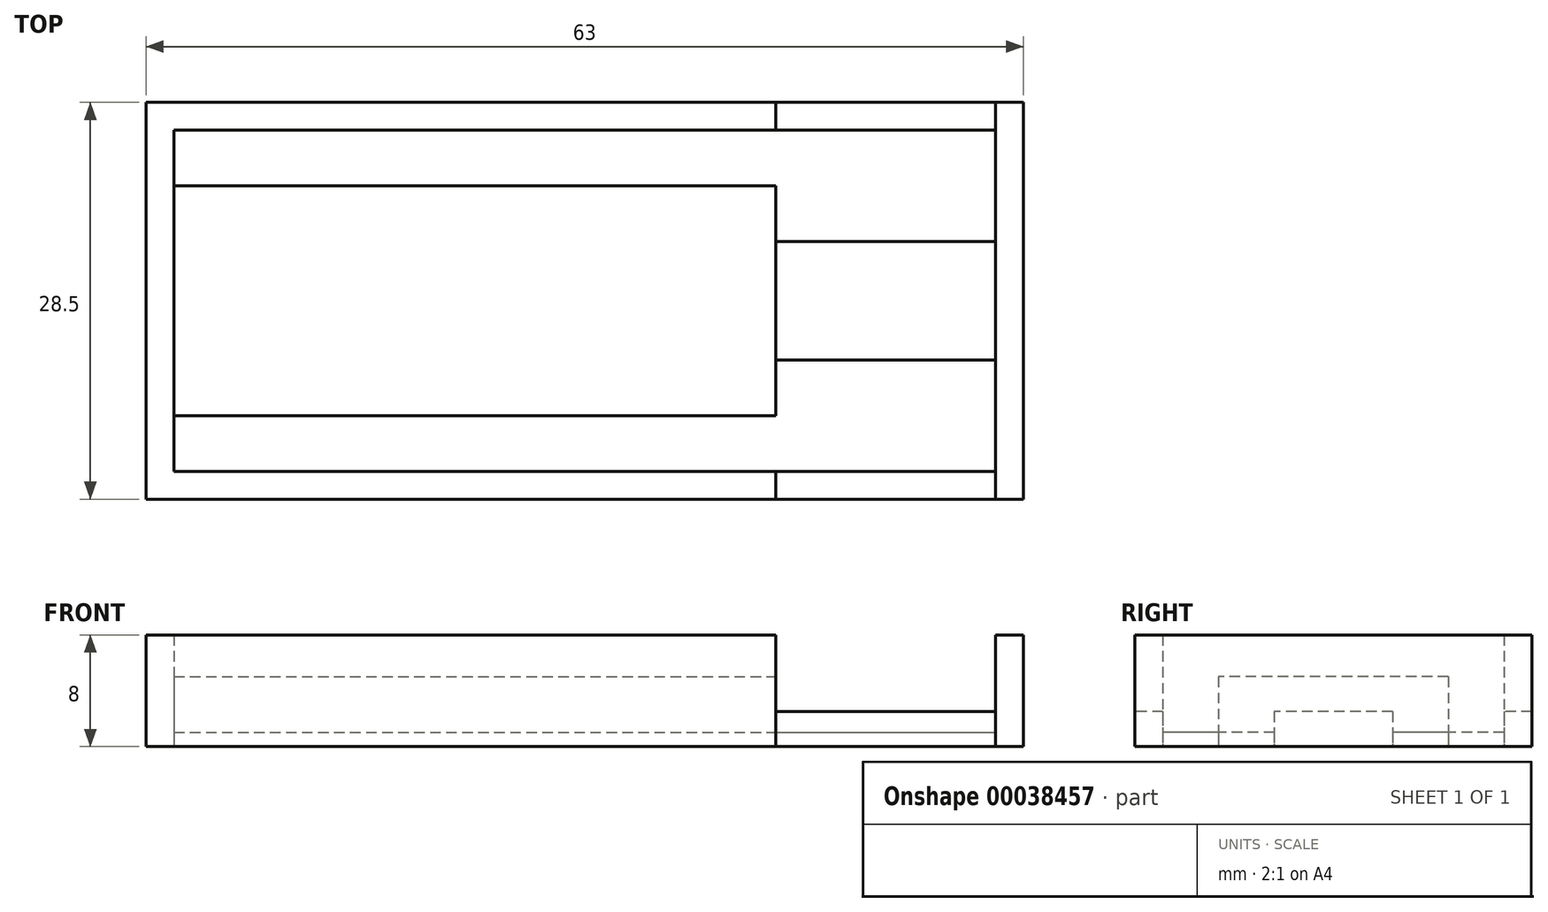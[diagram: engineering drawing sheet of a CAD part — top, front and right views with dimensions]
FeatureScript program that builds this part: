
annotation { "Feature Type Name" : "Feature", "Feature Type Description" : "" }
export const myFeature = defineFeature(function(context is Context, id is Id, definition is map)
    precondition{}
    {
        {
            var Q0;
            Q0=qCreatedBy(makeId("Top.planeOp"),FACE);
            var sketch = newSketch(context, id + "F0", { "sketchPlane" : qUnion([Q0])});
            skLineSegment(sketch, "E0", {"start": v(-83.28, 24.5) * mm, "end": v(93.04, 24.5) * mm, "construction": true});
            skLineSegment(sketch, "E1", {"start": v(59, -21.37) * mm, "end": v(59, 62.02) * mm, "construction": true});
            skLineSegment(sketch, "E2", {"start": v(-82.03, 20.5) * mm, "end": v(90.12, 20.5) * mm, "construction": true});
            skLineSegment(sketch, "E3", {"start": v(-82.58, 4) * mm, "end": v(90.12, 4) * mm, "construction": true});
            skLineSegment(sketch, "E4", {"start": v(43.2, 55.46) * mm, "end": v(43.2, -21.13) * mm, "construction": true});
            skLineSegment(sketch, "E5", {"start": v(-2, 34.22) * mm, "end": v(-2, -12.72) * mm, "construction": true});
            skLineSegment(sketch, "E6", {"start": v(-8.23, 26.5) * mm, "end": v(67.64, 26.5) * mm, "construction": true});
            skLineSegment(sketch, "E7", {"start": v(61, 36.16) * mm, "end": v(61, -15.62) * mm, "construction": true});
            skLineSegment(sketch, "E8", {"start": v(68.06, -2) * mm, "end": v(-8.92, -2) * mm, "construction": true});
            skLineSegment(sketch, "E9", {"start": v(34.9, 16.5) * mm, "end": v(73.13, 16.5) * mm, "construction": true});
            skLineSegment(sketch, "E10", {"start": v(34.68, 8) * mm, "end": v(73.78, 8) * mm, "construction": true});
            skLineSegment(sketch, "E11.bottom", {"start": v(59, 26.5) * mm, "end": v(61, 26.5) * mm});
            skLineSegment(sketch, "E11.top", {"start": v(59, -2) * mm, "end": v(61, -2) * mm});
            skLineSegment(sketch, "E11.left", {"start": v(59, 26.5) * mm, "end": v(59, -2) * mm});
            skLineSegment(sketch, "E11.right", {"start": v(61, 26.5) * mm, "end": v(61, -2) * mm});
            skLineSegment(sketch, "E12.bottom", {"start": v(43.2, 26.5) * mm, "end": v(59, 26.5) * mm});
            skLineSegment(sketch, "E12.top", {"start": v(43.2, 24.5) * mm, "end": v(59, 24.5) * mm});
            skLineSegment(sketch, "E12.left", {"start": v(43.2, 26.5) * mm, "end": v(43.2, 24.5) * mm});
            skLineSegment(sketch, "E12.right", {"start": v(59, 26.5) * mm, "end": v(59, 24.5) * mm});
            skLineSegment(sketch, "E13.top", {"start": v(43.2, 16.5) * mm, "end": v(59, 16.5) * mm});
            skLineSegment(sketch, "E13.left", {"start": v(43.2, 24.5) * mm, "end": v(43.2, 16.5) * mm});
            skLineSegment(sketch, "E13.right", {"start": v(59, 24.5) * mm, "end": v(59, 16.5) * mm});
            skLineSegment(sketch, "E14.top", {"start": v(43.2, 8) * mm, "end": v(59, 8) * mm});
            skLineSegment(sketch, "E14.left", {"start": v(43.2, 16.5) * mm, "end": v(43.2, 8) * mm});
            skLineSegment(sketch, "E14.right", {"start": v(59, 16.5) * mm, "end": v(59, 8) * mm});
            skLineSegment(sketch, "E15.top", {"start": v(43.2, 0) * mm, "end": v(59, 0) * mm});
            skLineSegment(sketch, "E15.left", {"start": v(43.2, 8) * mm, "end": v(43.2, 0) * mm});
            skLineSegment(sketch, "E15.right", {"start": v(59, 8) * mm, "end": v(59, 0) * mm});
            skLineSegment(sketch, "E16.top", {"start": v(43.2, -2) * mm, "end": v(59, -2) * mm});
            skLineSegment(sketch, "E16.left", {"start": v(43.2, 0) * mm, "end": v(43.2, -2) * mm});
            skLineSegment(sketch, "E16.right", {"start": v(59, 0) * mm, "end": v(59, -2) * mm});
            skLineSegment(sketch, "E17.bottom", {"start": v(0, 24.5) * mm, "end": v(43.2, 24.5) * mm});
            skLineSegment(sketch, "E17.top", {"start": v(0, 20.5) * mm, "end": v(43.2, 20.5) * mm});
            skLineSegment(sketch, "E17.left", {"start": v(0, 24.5) * mm, "end": v(0, 20.5) * mm});
            skLineSegment(sketch, "E17.right", {"start": v(43.2, 24.5) * mm, "end": v(43.2, 20.5) * mm});
            skLineSegment(sketch, "E18.top", {"start": v(0, 4) * mm, "end": v(43.2, 4) * mm});
            skLineSegment(sketch, "E18.left", {"start": v(0, 20.5) * mm, "end": v(0, 4) * mm});
            skLineSegment(sketch, "E18.right", {"start": v(43.2, 20.5) * mm, "end": v(43.2, 4) * mm});
            skLineSegment(sketch, "E19.top", {"start": v(0, 0) * mm, "end": v(43.2, 0) * mm});
            skLineSegment(sketch, "E19.left", {"start": v(0, 4) * mm, "end": v(0, 0) * mm});
            skLineSegment(sketch, "E19.right", {"start": v(43.2, 4) * mm, "end": v(43.2, 0) * mm});
            skLineSegment(sketch, "E20", {"start": v(43.2, 26.5) * mm, "end": v(-2, 26.5) * mm});
            skLineSegment(sketch, "E21", {"start": v(-2, 26.5) * mm, "end": v(-2, -2) * mm});
            skLineSegment(sketch, "E22", {"start": v(-2, -2) * mm, "end": v(43.2, -2) * mm});
            skSolve(sketch);
        }
        {
            var Q0;
            Q0=makeQuery(id+"F0.imprint","IMPRINT",FACE,{"disambiguationData":[TD([[makeQuery(id+"F0.imprint","IMPRINT",EDGE,{"derivedFrom":sQuery(id+"F0.wireOp",EDGE,"E12.top")}),-1.0]])]});
            var Q1;
            {var subQ1=sQuery(id+"F0.wireOp",EDGE,"E14.top");Q1=makeQuery(id+"F0.imprint","IMPRINT",FACE,{"disambiguationData":[TD([[makeQuery(id+"F0.imprint","IMPRINT",EDGE,{"derivedFrom":subQ1}),-1.0]])]});}
            var Q2;
            Q2=makeQuery(id+"F0.imprint","IMPRINT",FACE,{"disambiguationData":[TD([[makeQuery(id+"F0.imprint","IMPRINT",EDGE,{"derivedFrom":sQuery(id+"F0.wireOp",EDGE,"E17.bottom")}),-1.0]])]});
            var Q3;
            Q3=makeQuery(id+"F0.imprint","IMPRINT",FACE,{"disambiguationData":[TD([[makeQuery(id+"F0.imprint","IMPRINT",EDGE,{"derivedFrom":sQuery(id+"F0.wireOp",EDGE,"E18.top")}),-1.0]])]});
            extrude(context, id + "F1", {"entities" : qUnion([Q0, Q1, Q2, Q3]), "depth" : 1 * mm});
        }
        {
            var Q0;
            Q0=makeQuery(id+"F0.imprint","IMPRINT",FACE,{"disambiguationData":[TD([[makeQuery(id+"F0.imprint","IMPRINT",EDGE,{"derivedFrom":sQuery(id+"F0.wireOp",EDGE,"E12.bottom")}),-1.0]])]});
            var Q1;
            {var subQ0=sQuery(id+"F0.wireOp",EDGE,"E13.top");Q1=makeQuery(id+"F0.imprint","IMPRINT",FACE,{"disambiguationData":[TD([[makeQuery(id+"F0.imprint","IMPRINT",EDGE,{"derivedFrom":subQ0}),-1.0]])]});}
            var Q2;
            Q2=makeQuery(id+"F0.imprint","IMPRINT",FACE,{"disambiguationData":[TD([[makeQuery(id+"F0.imprint","IMPRINT",EDGE,{"derivedFrom":sQuery(id+"F0.wireOp",EDGE,"E15.top")}),-1.0]])]});
            extrude(context, id + "F2", {"entities" : qUnion([Q0, Q1, Q2]), "depth" : 2.5 * mm});
        }
        {
            var Q0;
            {var subQ4=sQuery(id+"F0.wireOp",EDGE,"E17.top");Q0=makeQuery(id+"F0.imprint","IMPRINT",FACE,{"disambiguationData":[TD([[makeQuery(id+"F0.imprint","IMPRINT",EDGE,{"derivedFrom":subQ4}),-1.0]])]});}
            extrude(context, id + "F3", {"entities" : qUnion([Q0]), "depth" : 5 * mm});
        }
        {
            var Q0;
            Q0=makeQuery(id+"F0.imprint","IMPRINT",FACE,{"disambiguationData":[TD([[makeQuery(id+"F0.imprint","IMPRINT",EDGE,{"derivedFrom":sQuery(id+"F0.wireOp",EDGE,"E12.left")}),-1.0]])]});
            var Q1;
            Q1=makeQuery(id+"F0.imprint","IMPRINT",FACE,{"disambiguationData":[TD([[makeQuery(id+"F0.imprint","IMPRINT",EDGE,{"derivedFrom":sQuery(id+"F0.wireOp",EDGE,"E11.bottom")}),-1.0]])]});
            extrude(context, id + "F4", {"entities" : qUnion([Q0, Q1]), "depth" : 8 * mm});
        }
    });
